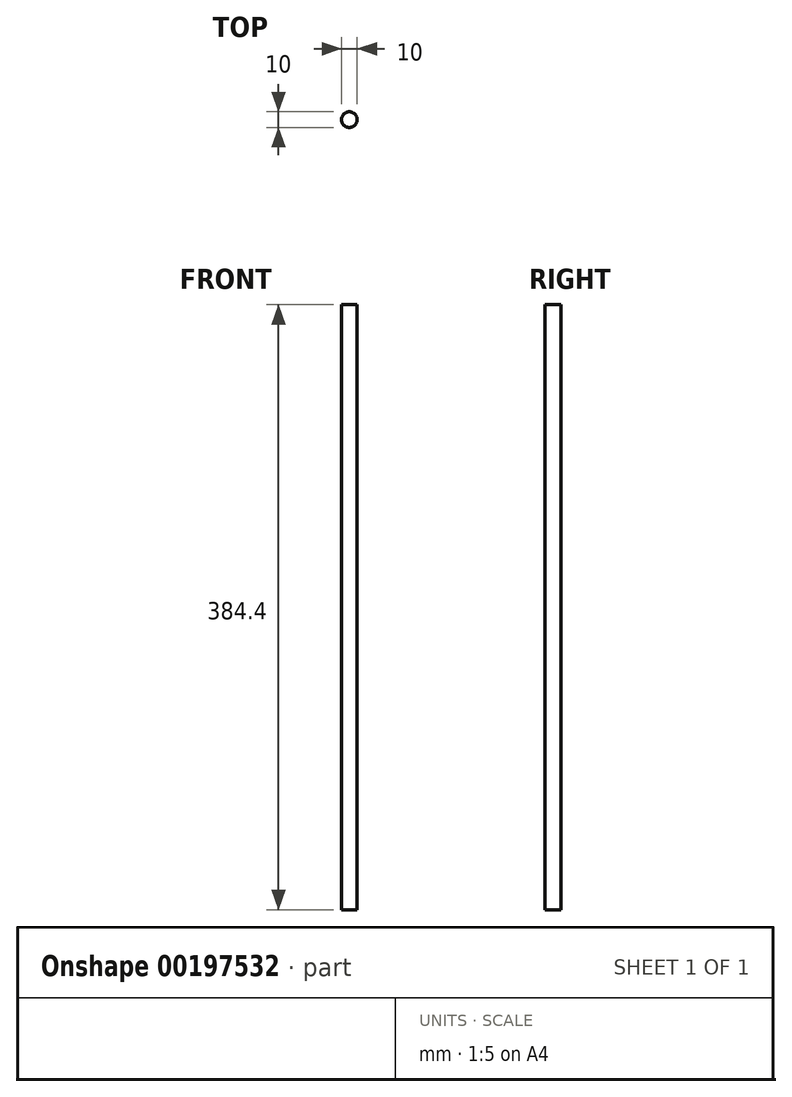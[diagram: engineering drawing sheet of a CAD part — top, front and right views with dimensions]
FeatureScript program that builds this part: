
annotation { "Feature Type Name" : "Feature", "Feature Type Description" : "" }
export const myFeature = defineFeature(function(context is Context, id is Id, definition is map)
    precondition{}
    {
        {
            var Q0;
            Q0=qCreatedBy(makeId("Top.planeOp"),FACE);
            var sketch = newSketch(context, id + "F0", { "sketchPlane" : qUnion([Q0])});
            skCircle(sketch, "E0", {"center": v(0, 0) * mm, "radius": 5 * mm});
            skSolve(sketch);
        }
        {
            var Q0;
            Q0=qSketchRegion(id+"F0",true);
            extrude(context, id + "F1", {"entities" : qUnion([Q0]), "depth" : 384.4 * mm});
        }
    });
